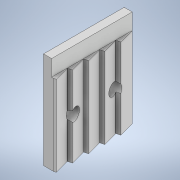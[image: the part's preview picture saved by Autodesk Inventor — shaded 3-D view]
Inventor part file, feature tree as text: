
AUTODESK INVENTOR PART (.ipt)
format: ipt  version: 2022 (Build 260153000, 153)  size: 153,088 bytes
history: native  units: mm
features: sketch x2, extrude x2, other x1, hole x1
ambient origin geometry x8: Origin, YZ Plane, XZ Plane, XY Plane, X Axis, Y Axis, Z Axis, Center Point
bodies: Body1 (feature_tree)
feature tree (6):
  other  "Sólido1"
  sketch  "Esboço1"  dims[d3=24.0mm d4=0.0mm d5=20.0mm d6=0.0mm]
  extrude  "Extrusão1"  Depth=20.0mm TaperAngle=0.0deg
  extrude  "Extrusão2"  [1 undecoded]
  hole  "Furo1"  [1 undecoded]
  sketch  "Esboço2"  dims[d7=3.0mm d8=6.0mm d9=4.0mm d10=2.0mm d11=90.0deg d12=8.0mm d13=20.594885mm]
note: 2 required parameter values undecoded (feature->parameter linkage not recoverable at this tier; creation-order binding heuristic only, values carry confidence <= 0.55)
